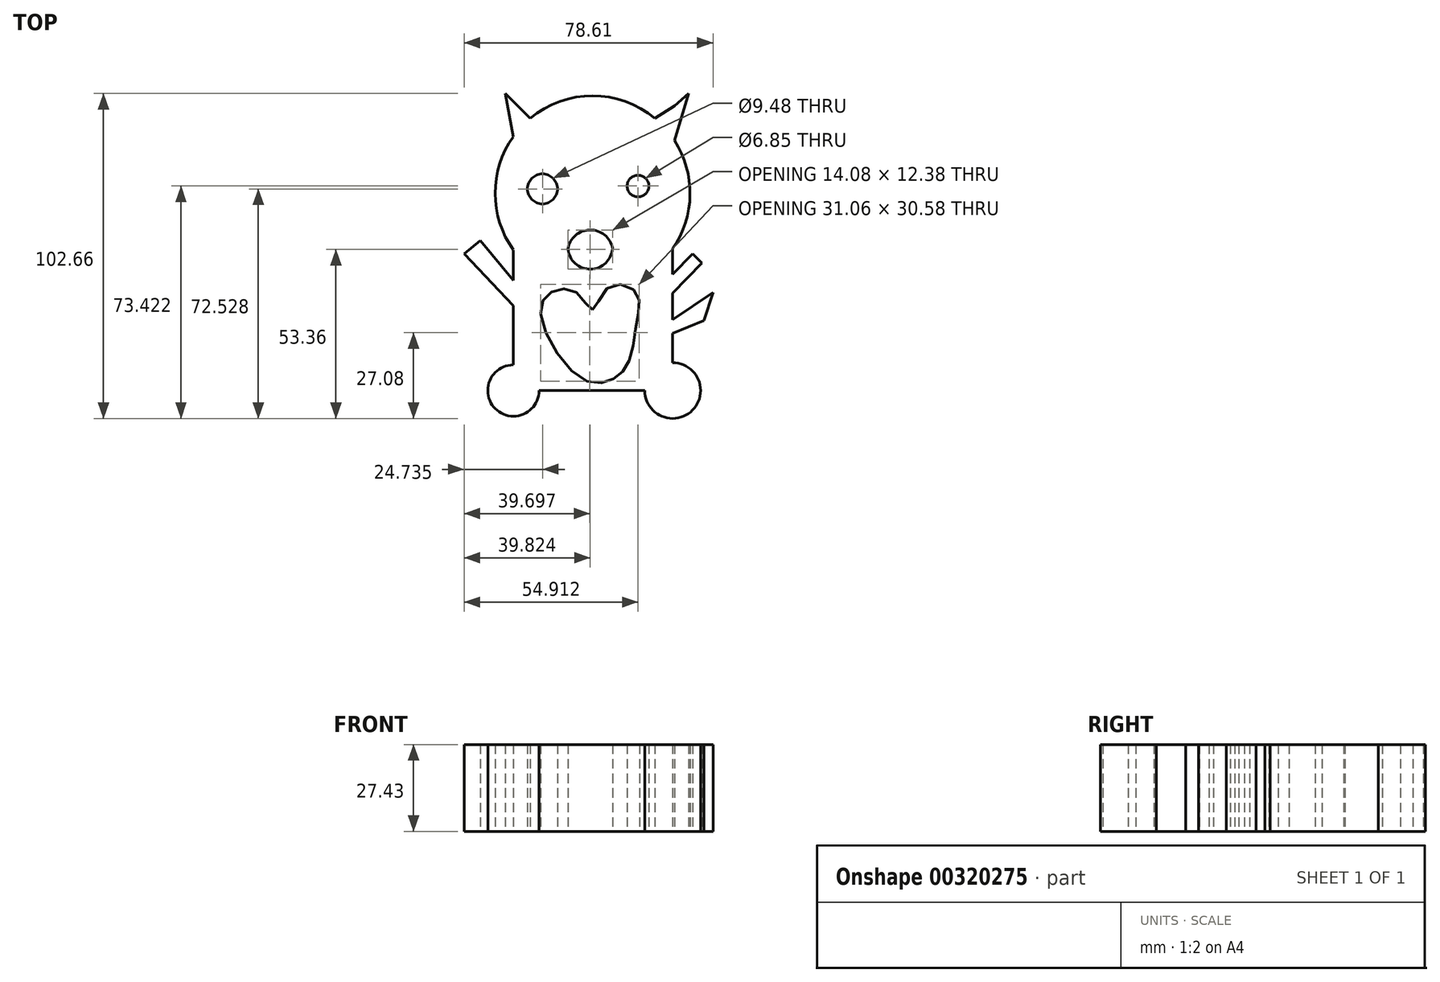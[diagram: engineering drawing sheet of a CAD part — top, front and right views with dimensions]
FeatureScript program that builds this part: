
annotation { "Feature Type Name" : "Feature", "Feature Type Description" : "" }
export const myFeature = defineFeature(function(context is Context, id is Id, definition is map)
    precondition{}
    {
        {
            var Q0;
            Q0=qCreatedBy(makeId("Top.planeOp"),FACE);
            var sketch = newSketch(context, id + "F0", { "sketchPlane" : qUnion([Q0])});
            skArc(sketch, "E0", {"start": v(25.3, 13.84) * mm, "mid": v(30.77, 30.84) * mm, "end": v(25.87, 48.01) * mm});
            skLineSegment(sketch, "E1", {"start": v(-25.06, 49.22) * mm, "end": v(-27.56, 62.85) * mm});
            skLineSegment(sketch, "E2", {"start": v(-27.56, 62.85) * mm, "end": v(-19.71, 54.98) * mm});
            skLineSegment(sketch, "E3", {"start": v(19.71, 54.98) * mm, "end": v(25.87, 58.92) * mm});
            skLineSegment(sketch, "E4", {"start": v(25.87, 58.92) * mm, "end": v(30.37, 62.85) * mm});
            skLineSegment(sketch, "E5", {"start": v(30.37, 62.85) * mm, "end": v(25.87, 48.01) * mm});
            skLineSegment(sketch, "E6", {"start": v(-25, 10.59) * mm, "end": v(-25, 3.88) * mm});
            skLineSegment(sketch, "E7", {"start": v(-20.98, -30.99) * mm, "end": v(-25, -30.99) * mm});
            skLineSegment(sketch, "E8", {"start": v(-17.85, -30.99) * mm, "end": v(25.3, -30.99) * mm});
            skLineSegment(sketch, "E9", {"start": v(25.3, -30.99) * mm, "end": v(25.3, -12.88) * mm});
            skLineSegment(sketch, "E10", {"start": v(-25, 10.59) * mm, "end": v(-25, 13.84) * mm});
            skCircle(sketch, "E11", {"center": v(-25, -30.99) * mm, "radius": 8.1 * mm});
            skCircle(sketch, "E12", {"center": v(25.3, -30.99) * mm, "radius": 8.82 * mm});
            skLineSegment(sketch, "E13", {"start": v(25.3, 5.7) * mm, "end": v(31.55, 12.15) * mm});
            skLineSegment(sketch, "E14", {"start": v(31.55, 12.15) * mm, "end": v(34.5, 9.3) * mm});
            skLineSegment(sketch, "E15", {"start": v(34.5, 9.3) * mm, "end": v(25.3, -0.2) * mm});
            skLineSegment(sketch, "E16", {"start": v(-25, 3.88) * mm, "end": v(-35.5, 16.4) * mm});
            skLineSegment(sketch, "E17", {"start": v(-35.5, 16.4) * mm, "end": v(-40.57, 12.15) * mm});
            skLineSegment(sketch, "E18", {"start": v(-40.57, 12.15) * mm, "end": v(-25, -4.17) * mm});
            skLineSegment(sketch, "E19", {"start": v(25.3, -8.58) * mm, "end": v(38.04, 0) * mm});
            skLineSegment(sketch, "E20", {"start": v(38.04, 0) * mm, "end": v(35.13, -8.86) * mm});
            skLineSegment(sketch, "E21", {"start": v(35.13, -8.86) * mm, "end": v(25.3, -12.88) * mm});
            skCircle(sketch, "E22", {"center": v(-15.84, 32.72) * mm, "radius": 4.74 * mm});
            skCircle(sketch, "E23", {"center": v(14.34, 33.61) * mm, "radius": 3.42 * mm});
            skArc(sketch, "E24", {"start": v(-7.79, 13.72) * mm, "mid": v(-0.64, 7.36) * mm, "end": v(6.3, 13.94) * mm});
            skArc(sketch, "E25", {"start": v(6.3, 13.94) * mm, "mid": v(-0.84, 19.74) * mm, "end": v(-7.79, 13.72) * mm});
            skLineSegment(sketch, "E26.trimOffspring", {"start": v(25.3, 5.7) * mm, "end": v(25.3, 13.84) * mm});
            skLineSegment(sketch, "E27.trimOffspring", {"start": v(25.3, -8.58) * mm, "end": v(25.3, -0.2) * mm});
            skLineSegment(sketch, "E28.trimOffspring", {"start": v(-25, -4.17) * mm, "end": v(-25, -30.99) * mm});
            skArc(sketch, "E29.trimOffspring", {"start": v(-25.06, 49.22) * mm, "mid": v(-30.77, 31.3) * mm, "end": v(-25, 13.42) * mm});
            skArc(sketch, "E30.trimOffspring", {"start": v(19.71, 54.98) * mm, "mid": v(0, 62.13) * mm, "end": v(-19.71, 54.98) * mm});
            skPoint(sketch, "E31.end.orphan", {"position": v(30.37, 36.3) * mm});
            skPoint(sketch, "E32.end.orphan", {"position": v(8.08, 3.3) * mm});
            skPoint(sketch, "E33.orphan", {"position": v(8.08, 1.67) * mm});
            skFitSpline(sketch, "E34", {"points": [v(0, -5.48) * mm, v(-5.06, 0) * mm, v(-13.22, 0) * mm, v(-16.31, -7.17) * mm, v(-3.66, -27.14) * mm, v(6.19, -27.42) * mm, v(11.25, -22.08) * mm, v(14.06, -8.86) * mm, v(13.78, 0) * mm, v(5.06, 1.67) * mm, v(0, -5.48) * mm]});
            skSolve(sketch);
        }
        {
            var Q0;
            {var subQ0=sQuery(id+"F0.wireOp",EDGE,"E31");Q0=makeQuery(id+"F0.imprint","IMPRINT",FACE,{"disambiguationData":[TD([[makeQuery(id+"F0.imprint","IMPRINT",EDGE,{"derivedFrom":subQ0}),1.0]])]});}
            var Q1;
            {var subQ0=sQuery(id+"F0.wireOp",EDGE,"E3");Q1=makeQuery(id+"F0.imprint","IMPRINT",FACE,{"disambiguationData":[TD([[makeQuery(id+"F0.imprint","IMPRINT",EDGE,{"derivedFrom":subQ0}),-1.0]])]});}
            var Q2;
            {var subQ0=sQuery(id+"F0.wireOp",EDGE,"E1");Q2=makeQuery(id+"F0.imprint","IMPRINT",FACE,{"disambiguationData":[TD([[makeQuery(id+"F0.imprint","IMPRINT",EDGE,{"derivedFrom":subQ0}),-1.0]])]});}
            var Q3;
            {var subQ0=sQuery(id+"F0.wireOp",EDGE,"E16");Q3=makeQuery(id+"F0.imprint","IMPRINT",FACE,{"disambiguationData":[TD([[makeQuery(id+"F0.imprint","IMPRINT",EDGE,{"derivedFrom":subQ0}),1.0]])]});}
            var Q4;
            {var subQ0=sQuery(id+"F0.wireOp",EDGE,"E9");var subQ1=sQuery(id+"F0.wireOp",EDGE,"E8");var subQ2=makeQuery(id+"F0.imprint","INTERSECT",VERTEX,{"derivedFrom":[subQ1,subQ0]});Q4=makeQuery(id+"F0.imprint","IMPRINT",FACE,{"disambiguationData":[TD([[makeQuery(id+"F0.imprint","IMPRINT",EDGE,{"disambiguationData":[TD([[subQ2,1.0]])],"derivedFrom":subQ1}),-1.0]])]});}
            var Q5;
            {var subQ0=sQuery(id+"F0.wireOp",EDGE,"E19");Q5=makeQuery(id+"F0.imprint","IMPRINT",FACE,{"disambiguationData":[TD([[makeQuery(id+"F0.imprint","IMPRINT",EDGE,{"derivedFrom":subQ0}),-1.0]])]});}
            var Q6;
            {var subQ0=sQuery(id+"F0.wireOp",EDGE,"E13");Q6=makeQuery(id+"F0.imprint","IMPRINT",FACE,{"disambiguationData":[TD([[makeQuery(id+"F0.imprint","IMPRINT",EDGE,{"derivedFrom":subQ0}),-1.0]])]});}
            var Q7;
            {var subQ0=sQuery(id+"F0.wireOp",EDGE,"E11");var subQ1=makeQuery(id+"F0.imprint","INTERSECT",VERTEX,{"derivedFrom":[sQuery(id+"F0.wireOp",EDGE,"E6"),subQ0]});Q7=makeQuery(id+"F0.imprint","IMPRINT",FACE,{"disambiguationData":[TD([[makeQuery(id+"F0.imprint","IMPRINT",EDGE,{"disambiguationData":[TD([[subQ1,1.0]])],"derivedFrom":subQ0}),1.0]])]});}
            var Q8;
            {var subQ0=sQuery(id+"F0.wireOp",EDGE,"E9");var subQ1=sQuery(id+"F0.wireOp",EDGE,"E8");var subQ2=makeQuery(id+"F0.imprint","INTERSECT",VERTEX,{"derivedFrom":[subQ1,subQ0]});Q8=makeQuery(id+"F0.imprint","IMPRINT",FACE,{"disambiguationData":[TD([[makeQuery(id+"F0.imprint","IMPRINT",EDGE,{"disambiguationData":[TD([[subQ2,1.0]])],"derivedFrom":subQ1}),1.0]])]});}
            var Q9;
            {var subQ9=sQuery(id+"F0.wireOp",EDGE,"E0");var subQ10=makeQuery(id+"F0.imprint","IMPRINT",VERTEX,{"disambiguationData":[OD(0.0)],"derivedFrom":subQ9});Q9=makeQuery(id+"F0.imprint","IMPRINT",FACE,{"disambiguationData":[TD([[makeQuery(id+"F0.imprint","IMPRINT",EDGE,{"disambiguationData":[TD([[subQ10,-1.0]])],"derivedFrom":subQ9}),-1.0]])]});}
            extrude(context, id + "F1", {"entities" : qUnion([Q0, Q1, Q2, Q3, Q4, Q5, Q6, Q7, Q8, Q9]), "depth" : 27.43 * mm});
        }
    });
